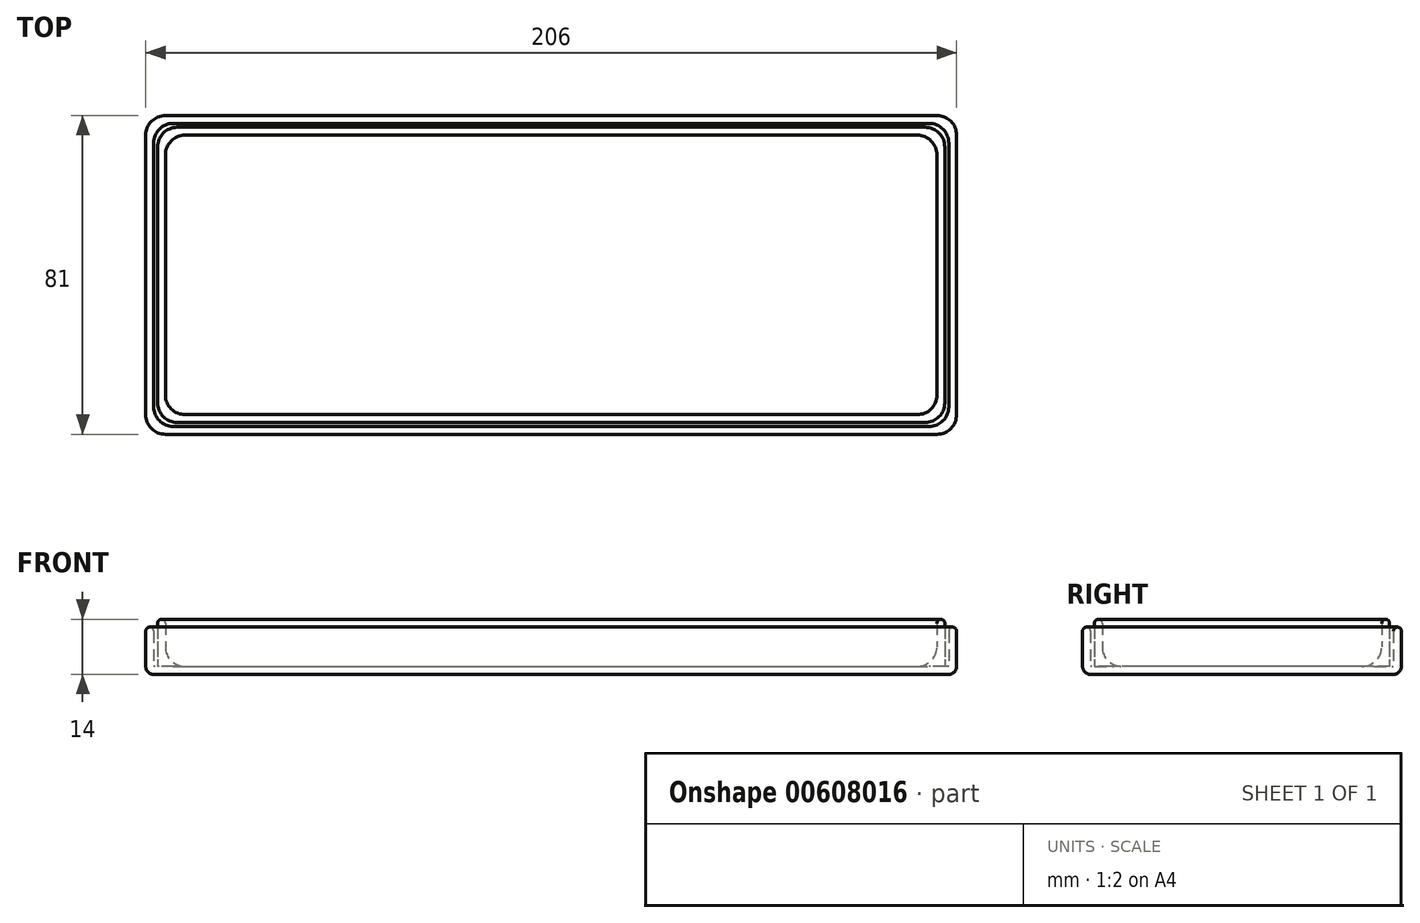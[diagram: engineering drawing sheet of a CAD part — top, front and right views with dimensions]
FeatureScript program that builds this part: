
annotation { "Feature Type Name" : "Feature", "Feature Type Description" : "" }
export const myFeature = defineFeature(function(context is Context, id is Id, definition is map)
    precondition{}
    {
        {
            var Q0;
            Q0=qCreatedBy(makeId("Top.planeOp"),FACE);
            var sketch = newSketch(context, id + "F0", { "sketchPlane" : qUnion([Q0])});
            skLineSegment(sketch, "E0.bottom", {"start": v(103, -40.5) * mm, "end": v(-103, -40.5) * mm});
            skLineSegment(sketch, "E0.top", {"start": v(103, 40.5) * mm, "end": v(-103, 40.5) * mm});
            skLineSegment(sketch, "E0.left", {"start": v(103, -40.5) * mm, "end": v(103, 40.5) * mm});
            skLineSegment(sketch, "E0.right", {"start": v(-103, -40.5) * mm, "end": v(-103, 40.5) * mm});
            skPoint(sketch, "E0.middle", {"position": v(0, 0) * mm});
            skSolve(sketch);
        }
        {
            var Q0;
            Q0=makeQuery(id+"F0.imprint","IMPRINT",FACE,{"disambiguationData":[TD([[makeQuery(id+"F0.imprint","IMPRINT",EDGE,{"derivedFrom":sQuery(id+"F0.wireOp",EDGE,"E0.bottom")}),-1.0]])]});
            extrude(context, id + "F1", {"entities" : qUnion([Q0]), "depth" : 2 * mm, "offsetDistance" : 25 * mm});
        }
        {
            var Q0;
            Q0=makeQuery(id+"F1.opExtrude","CAP_FACE",FACE,{"disambiguationData":[OSD([sQuery(id+"F0.wireOp",EDGE,"E0.bottom"),sQuery(id+"F0.wireOp",EDGE,"E0.top"),sQuery(id+"F0.wireOp",EDGE,"E0.left"),sQuery(id+"F0.wireOp",EDGE,"E0.right")])],"isStart":false});
            var sketch = newSketch(context, id + "F2", { "sketchPlane" : qUnion([Q0])});
            skLineSegment(sketch, "E1.bottom", {"start": v(-101, 38.5) * mm, "end": v(101, 38.5) * mm});
            skLineSegment(sketch, "E1.top", {"start": v(-101, -38.5) * mm, "end": v(101, -38.5) * mm});
            skLineSegment(sketch, "E1.left", {"start": v(-101, 38.5) * mm, "end": v(-101, -38.5) * mm});
            skLineSegment(sketch, "E1.right", {"start": v(101, 38.5) * mm, "end": v(101, -38.5) * mm});
            skPoint(sketch, "E1.middle", {"position": v(0, 0) * mm});
            skLineSegment(sketch, "E2.bottom", {"start": v(-100, 37.5) * mm, "end": v(100, 37.5) * mm});
            skLineSegment(sketch, "E2.top", {"start": v(-100, -37.5) * mm, "end": v(100, -37.5) * mm});
            skLineSegment(sketch, "E2.left", {"start": v(-100, 37.5) * mm, "end": v(-100, -37.5) * mm});
            skLineSegment(sketch, "E2.right", {"start": v(100, 37.5) * mm, "end": v(100, -37.5) * mm});
            skLineSegment(sketch, "E3.bottom", {"start": v(-98, 35.5) * mm, "end": v(98, 35.5) * mm});
            skLineSegment(sketch, "E3.top", {"start": v(-98, -35.5) * mm, "end": v(98, -35.5) * mm});
            skLineSegment(sketch, "E3.left", {"start": v(-98, 35.5) * mm, "end": v(-98, -35.5) * mm});
            skLineSegment(sketch, "E3.right", {"start": v(98, 35.5) * mm, "end": v(98, -35.5) * mm});
            skLineSegment(sketch, "E4", {"start": v(100, -23.72) * mm, "end": v(101, -23.72) * mm, "construction": true});
            skSolve(sketch);
        }
        {
            var Q0;
            Q0=makeQuery(id+"F2.imprint","IMPRINT",FACE,{"disambiguationData":[TD([[makeQuery(id+"F2.imprint","IMPRINT",EDGE,{"derivedFrom":sQuery(id+"F2.wireOp",EDGE,"E2.bottom")}),-1.0]])]});
            extrude(context, id + "F3", {"entities" : qUnion([Q0]), "operationType" : NewBodyOperationType.ADD, "depth" : 12 * mm, "offsetDistance" : 25 * mm});
        }
        {
            var Q0;
            Q0=makeQuery(id+"F2.imprint","IMPRINT",FACE,{"disambiguationData":[TD([[makeQuery(id+"F2.imprint","IMPRINT",EDGE,{"derivedFrom":sQuery(id+"F2.wireOp",EDGE,"E1.bottom")}),1.0]])]});
            extrude(context, id + "F4", {"entities" : qUnion([Q0]), "operationType" : NewBodyOperationType.ADD, "depth" : 10 * mm, "offsetDistance" : 25 * mm});
        }
        {
            var Q0;
            Q0=makeQuery(id+"F3.opExtrude","SWEPT_EDGE",EDGE,{"disambiguationData":[OSD([sQuery(id+"F2.wireOp",EDGE,"E2.top"),sQuery(id+"F2.wireOp",EDGE,"E2.left")])]});
            var Q1;
            Q1=makeQuery(id+"F3.opExtrude","SWEPT_EDGE",EDGE,{"disambiguationData":[OSD([sQuery(id+"F2.wireOp",EDGE,"E2.bottom"),sQuery(id+"F2.wireOp",EDGE,"E2.left")])]});
            var Q2;
            Q2=makeQuery(id+"F3.opExtrude","SWEPT_EDGE",EDGE,{"disambiguationData":[OSD([sQuery(id+"F2.wireOp",EDGE,"E2.bottom"),sQuery(id+"F2.wireOp",EDGE,"E2.right")])]});
            var Q3;
            Q3=makeQuery(id+"F3.opExtrude","SWEPT_EDGE",EDGE,{"disambiguationData":[OSD([sQuery(id+"F2.wireOp",EDGE,"E2.top"),sQuery(id+"F2.wireOp",EDGE,"E2.right")])]});
            fillet(context, id + "F5", {"entities" : qUnion([Q0, Q1, Q2, Q3]), "radius" : 5 * mm, "tangentPropagation" : true, "allowEdgeOverflow" : false});
        }
        {
            var Q0;
            Q0=makeQuery(id+"F3.opExtrude","SWEPT_EDGE",EDGE,{"disambiguationData":[OSD([sQuery(id+"F2.wireOp",EDGE,"E3.top"),sQuery(id+"F2.wireOp",EDGE,"E3.left")])]});
            var Q1;
            Q1=makeQuery(id+"F3.opExtrude","SWEPT_EDGE",EDGE,{"disambiguationData":[OSD([sQuery(id+"F2.wireOp",EDGE,"E3.bottom"),sQuery(id+"F2.wireOp",EDGE,"E3.left")])]});
            var Q2;
            Q2=makeQuery(id+"F3.opExtrude","SWEPT_EDGE",EDGE,{"disambiguationData":[OSD([sQuery(id+"F2.wireOp",EDGE,"E3.bottom"),sQuery(id+"F2.wireOp",EDGE,"E3.right")])]});
            var Q3;
            Q3=makeQuery(id+"F3.opExtrude","SWEPT_EDGE",EDGE,{"disambiguationData":[OSD([sQuery(id+"F2.wireOp",EDGE,"E3.top"),sQuery(id+"F2.wireOp",EDGE,"E3.right")])]});
            fillet(context, id + "F6", {"entities" : qUnion([Q0, Q1, Q2, Q3]), "radius" : 5 * mm, "tangentPropagation" : true, "allowEdgeOverflow" : false});
        }
        {
            var Q0;
            Q0=makeQuery(id+"F3.opExtrude","CAP_FACE",FACE,{"disambiguationData":[OSD([sQuery(id+"F2.wireOp",EDGE,"E2.bottom"),sQuery(id+"F2.wireOp",EDGE,"E2.top"),sQuery(id+"F2.wireOp",EDGE,"E2.left"),sQuery(id+"F2.wireOp",EDGE,"E2.right"),sQuery(id+"F2.wireOp",EDGE,"E3.bottom"),sQuery(id+"F2.wireOp",EDGE,"E3.top"),sQuery(id+"F2.wireOp",EDGE,"E3.left"),sQuery(id+"F2.wireOp",EDGE,"E3.right")])],"isStart":false});
            fillet(context, id + "F7", {"entities" : qUnion([Q0]), "radius" : 1 * mm, "tangentPropagation" : true, "allowEdgeOverflow" : false});
        }
        {
            var Q0;
            Q0=makeQuery(id+"F4.opExtrude","SWEPT_EDGE",EDGE,{"disambiguationData":[OSD([sQuery(id+"F2.wireOp",EDGE,"E1.bottom"),sQuery(id+"F2.wireOp",EDGE,"E1.left")])]});
            var Q1;
            Q1=makeQuery(id+"F4.opExtrude","SWEPT_EDGE",EDGE,{"disambiguationData":[OSD([sQuery(id+"F2.wireOp",EDGE,"E1.top"),sQuery(id+"F2.wireOp",EDGE,"E1.left")])]});
            var Q2;
            Q2=makeQuery(id+"F4.opExtrude","SWEPT_EDGE",EDGE,{"disambiguationData":[OSD([sQuery(id+"F2.wireOp",EDGE,"E1.top"),sQuery(id+"F2.wireOp",EDGE,"E1.right")])]});
            var Q3;
            Q3=makeQuery(id+"F4.opExtrude","SWEPT_EDGE",EDGE,{"disambiguationData":[OSD([sQuery(id+"F2.wireOp",EDGE,"E1.bottom"),sQuery(id+"F2.wireOp",EDGE,"E1.right")])]});
            fillet(context, id + "F8", {"entities" : qUnion([Q0, Q1, Q2, Q3]), "radius" : 5 * mm, "tangentPropagation" : true, "allowEdgeOverflow" : false});
        }
        {
            var Q0;
            {var subQ0=sQuery(id+"F0.wireOp",EDGE,"E0.right");var subQ1=sQuery(id+"F0.wireOp",EDGE,"E0.bottom");Q0=makeQuery(id+"F4.boolean.opBoolean","MERGE",EDGE,{"derivedFrom":[makeQuery(id+"F1.opExtrude","SWEPT_EDGE",EDGE,{"disambiguationData":[OSD([subQ1,subQ0])]}),makeQuery(id+"F4.opExtrude","SWEPT_EDGE",EDGE,{"disambiguationData":[OSD([subQ1,subQ0])]})]});}
            var Q1;
            {var subQ0=sQuery(id+"F0.wireOp",EDGE,"E0.left");var subQ1=sQuery(id+"F0.wireOp",EDGE,"E0.bottom");Q1=makeQuery(id+"F4.boolean.opBoolean","MERGE",EDGE,{"derivedFrom":[makeQuery(id+"F1.opExtrude","SWEPT_EDGE",EDGE,{"disambiguationData":[OSD([subQ1,subQ0])]}),makeQuery(id+"F4.opExtrude","SWEPT_EDGE",EDGE,{"disambiguationData":[OSD([subQ1,subQ0])]})]});}
            var Q2;
            {var subQ0=sQuery(id+"F0.wireOp",EDGE,"E0.left");var subQ1=sQuery(id+"F0.wireOp",EDGE,"E0.top");Q2=makeQuery(id+"F4.boolean.opBoolean","MERGE",EDGE,{"derivedFrom":[makeQuery(id+"F1.opExtrude","SWEPT_EDGE",EDGE,{"disambiguationData":[OSD([subQ1,subQ0])]}),makeQuery(id+"F4.opExtrude","SWEPT_EDGE",EDGE,{"disambiguationData":[OSD([subQ1,subQ0])]})]});}
            var Q3;
            {var subQ0=sQuery(id+"F0.wireOp",EDGE,"E0.right");var subQ1=sQuery(id+"F0.wireOp",EDGE,"E0.top");Q3=makeQuery(id+"F4.boolean.opBoolean","MERGE",EDGE,{"derivedFrom":[makeQuery(id+"F1.opExtrude","SWEPT_EDGE",EDGE,{"disambiguationData":[OSD([subQ1,subQ0])]}),makeQuery(id+"F4.opExtrude","SWEPT_EDGE",EDGE,{"disambiguationData":[OSD([subQ1,subQ0])]})]});}
            fillet(context, id + "F9", {"entities" : qUnion([Q0, Q1, Q2, Q3]), "radius" : 5 * mm, "tangentPropagation" : true, "allowEdgeOverflow" : false});
        }
        {
            var Q0;
            Q0=makeQuery(id+"F1.opExtrude","CAP_FACE",FACE,{"disambiguationData":[OSD([sQuery(id+"F0.wireOp",EDGE,"E0.bottom"),sQuery(id+"F0.wireOp",EDGE,"E0.top"),sQuery(id+"F0.wireOp",EDGE,"E0.left"),sQuery(id+"F0.wireOp",EDGE,"E0.right")])],"isStart":true});
            fillet(context, id + "F10", {"entities" : qUnion([Q0]), "radius" : 2 * mm, "tangentPropagation" : true, "allowEdgeOverflow" : false});
        }
        {
            var Q0;
            Q0=makeQuery(id+"F4.opExtrude","CAP_FACE",FACE,{"disambiguationData":[OSD([sQuery(id+"F0.wireOp",EDGE,"E0.bottom"),sQuery(id+"F0.wireOp",EDGE,"E0.top"),sQuery(id+"F0.wireOp",EDGE,"E0.left"),sQuery(id+"F0.wireOp",EDGE,"E0.right"),sQuery(id+"F2.wireOp",EDGE,"E1.bottom"),sQuery(id+"F2.wireOp",EDGE,"E1.top"),sQuery(id+"F2.wireOp",EDGE,"E1.left"),sQuery(id+"F2.wireOp",EDGE,"E1.right")])],"isStart":false});
            fillet(context, id + "F11", {"entities" : qUnion([Q0]), "radius" : 1 * mm, "tangentPropagation" : true, "allowEdgeOverflow" : false});
        }
        {
            var Q0;
            Q0=makeQuery(id+"F3.boolean.opBoolean","SPLIT",FACE,{"disambiguationData":[TD([makeQuery(id+"F3.opExtrude","SWEPT_FACE",FACE,{"disambiguationData":[OSD([sQuery(id+"F2.wireOp",EDGE,"E3.bottom")])]})])],"derivedFrom":makeQuery(id+"F1.opExtrude","CAP_FACE",FACE,{"disambiguationData":[OSD([sQuery(id+"F0.wireOp",EDGE,"E0.bottom"),sQuery(id+"F0.wireOp",EDGE,"E0.top"),sQuery(id+"F0.wireOp",EDGE,"E0.left"),sQuery(id+"F0.wireOp",EDGE,"E0.right")])],"isStart":false})});
            fillet(context, id + "F12", {"entities" : qUnion([Q0]), "radius" : 5 * mm, "tangentPropagation" : true, "allowEdgeOverflow" : false});
        }
    });
